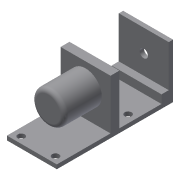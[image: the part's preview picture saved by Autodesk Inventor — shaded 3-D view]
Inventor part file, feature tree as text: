
AUTODESK INVENTOR PART (.ipt)
format: ipt  version: 2015 (Build 190159000, 159)  size: 148,480 bytes
history: native  units: in
note: dims shown in document units (in); Inventor stores cm internally (conversion verified against a paired STEP export)
features: sketch x8, extrude x7, mirror x2, fillet x1
ambient origin geometry x8: Origin, YZ Plane, XZ Plane, XY Plane, X Axis, Y Axis, Z Axis, Center Point
bodies: Solid1 (feature_tree)
feature tree (18):
  extrude  "Extrusion1"  Depth=0.25in TaperAngle=0.0deg
  extrude  "Extrusion2"  Depth=0.5in TaperAngle=0.0deg
  extrude  "Extrusion3"  Depth=0.5in TaperAngle=0.0deg
  extrude  "Extrusion4"  Depth=0.25in
  extrude  "Extrusion5"  Depth=1.0in TaperAngle=0.0deg
  fillet  "Fillet1"  [1 undecoded]
  extrude  "Extrusion6"  [1 undecoded]
  mirror  "Mirror1"
  extrude  "Extrusion7"  [1 undecoded]
  mirror  "Mirror2"
  sketch  "Sketch8"
  sketch  "Sketch1"  dims[d0=3.0in d1=0.25in d2=0.0in]
  sketch  "Sketch2"  dims[d3=3.0in d4=0.0in d5=0.5in d6=0.0in]
  sketch  "Sketch3"  dims[d7=0.5in d8=3.9375in d9=0.0in]
  sketch  "Sketch4"  dims[d10=2.25in d11=0.0in d12=0.25in]
  sketch  "Sketch5"  dims[d13=1.0in d14=0.0in d15=1.0in d16=0.0in]
  sketch  "Sketch6"
  sketch  "Sketch7"
note: 3 required parameter values undecoded (feature->parameter linkage not recoverable at this tier; creation-order binding heuristic only, values carry confidence <= 0.55)
